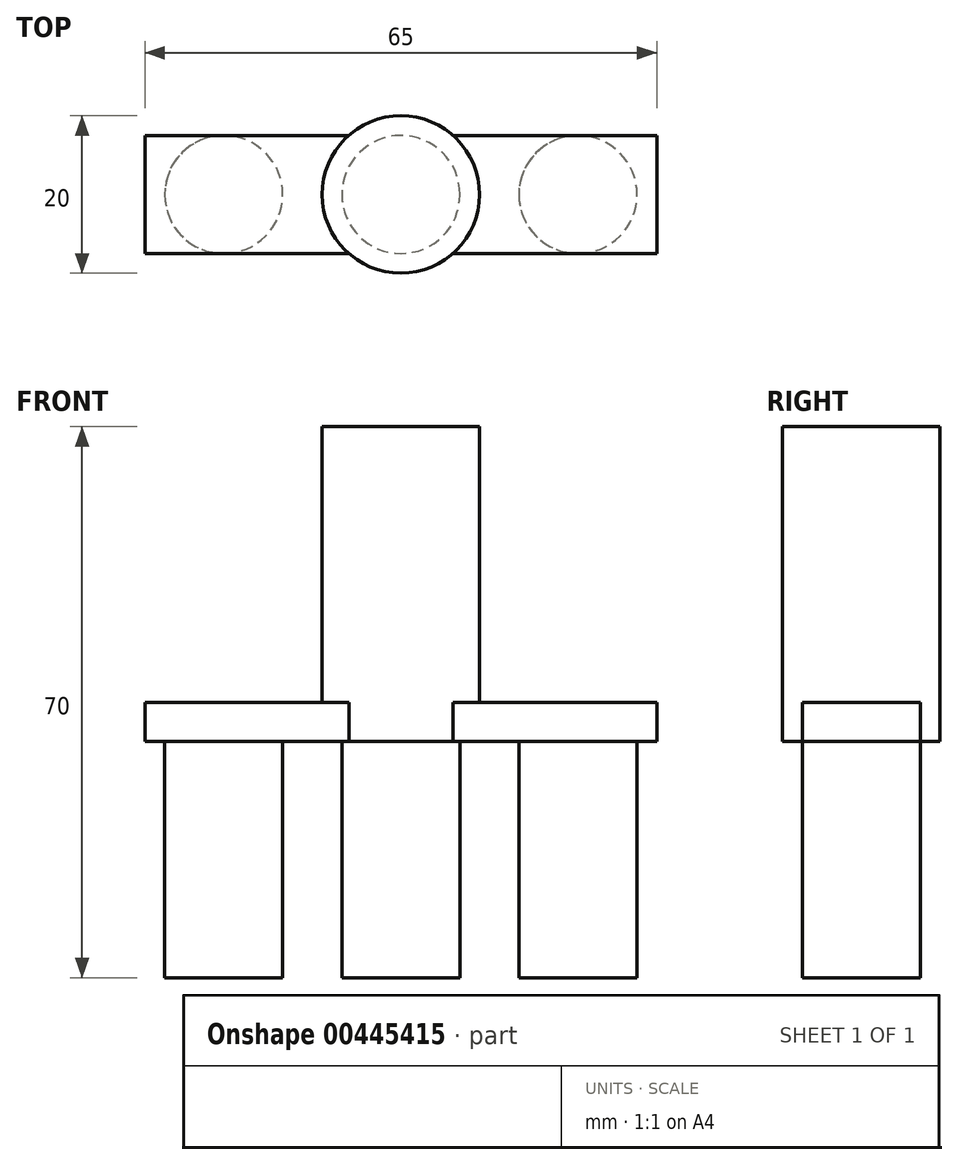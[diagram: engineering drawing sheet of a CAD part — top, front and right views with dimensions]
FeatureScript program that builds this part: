
annotation { "Feature Type Name" : "Feature", "Feature Type Description" : "" }
export const myFeature = defineFeature(function(context is Context, id is Id, definition is map)
    precondition{}
    {
        {
            var Q0;
            Q0=qCreatedBy(makeId("Top.planeOp"),FACE);
            var sketch = newSketch(context, id + "F0", { "sketchPlane" : qUnion([Q0])});
            skLineSegment(sketch, "E0.bottom", {"start": v(32.5, 7.5) * mm, "end": v(-32.5, 7.5) * mm});
            skLineSegment(sketch, "E0.top", {"start": v(32.5, -7.5) * mm, "end": v(-32.5, -7.5) * mm});
            skLineSegment(sketch, "E0.left", {"start": v(32.5, 7.5) * mm, "end": v(32.5, -7.5) * mm});
            skLineSegment(sketch, "E0.right", {"start": v(-32.5, 7.5) * mm, "end": v(-32.5, -7.5) * mm});
            skPoint(sketch, "E0.middle", {"position": v(0, 0) * mm});
            skSolve(sketch);
        }
        {
            var Q0;
            {var subQ5=sQuery(id+"F0.wireOp",EDGE,"E0.right");Q0=makeQuery(id+"F0.imprint","IMPRINT",FACE,{"disambiguationData":[TD([[makeQuery(id+"F0.imprint","IMPRINT",EDGE,{"derivedFrom":subQ5}),1.0]])]});}
            var Q1;
            {var subQ5=sQuery(id+"F0.wireOp",EDGE,"E0.left");Q1=makeQuery(id+"F0.imprint","IMPRINT",FACE,{"disambiguationData":[TD([[makeQuery(id+"F0.imprint","IMPRINT",EDGE,{"derivedFrom":subQ5}),-1.0]])]});}
            extrude(context, id + "F1", {"entities" : qUnion([Q0, Q1]), "oppositeDirection" : true, "depth" : 5 * mm});
        }
        {
            var Q0;
            Q0=makeQuery(id+"F1.opExtrude","CAP_FACE",FACE,{"disambiguationData":[OSD([sQuery(id+"F0.wireOp",EDGE,"E0.bottom"),sQuery(id+"F0.wireOp",EDGE,"E0.top"),sQuery(id+"F0.wireOp",EDGE,"E0.left"),sQuery(id+"F0.wireOp",EDGE,"E0.right")])],"isStart":false});
            var sketch = newSketch(context, id + "F2", { "sketchPlane" : qUnion([Q0])});
            skCircle(sketch, "E1", {"center": v(0, 0) * mm, "radius": 10 * mm});
            skSolve(sketch);
        }
        {
            var Q0;
            Q0 = qSketchRegion(id + "F2", true);
            extrude(context, id + "F3", {"entities" : qUnion([Q0]), "operationType" : NewBodyOperationType.ADD, "oppositeDirection" : true, "depth" : 40 * mm});
        }
        {
            var Q0;
            Q0=makeQuery(id+"F3.boolean.opBoolean","MERGE",FACE,{"derivedFrom":[makeQuery(id+"F1.opExtrude","CAP_FACE",FACE,{"disambiguationData":[OSD([sQuery(id+"F0.wireOp",EDGE,"E0.bottom"),sQuery(id+"F0.wireOp",EDGE,"E0.top"),sQuery(id+"F0.wireOp",EDGE,"E0.left"),sQuery(id+"F0.wireOp",EDGE,"E0.right")])],"isStart":false}),makeQuery(id+"F3.opExtrude","CAP_FACE",FACE,{"disambiguationData":[OSD([sQuery(id+"F2.wireOp",EDGE,"E1")])],"isStart":true})]});
            var sketch = newSketch(context, id + "F4", { "sketchPlane" : qUnion([Q0])});
            skCircle(sketch, "E2", {"center": v(0, 0) * mm, "radius": 7.5 * mm});
            skLineSegment(sketch, "E3", {"start": v(-7.5, 0) * mm, "end": v(-22.5, 0) * mm});
            skLineSegment(sketch, "E4", {"start": v(7.5, 0) * mm, "end": v(22.5, 0) * mm});
            skCircle(sketch, "E5", {"center": v(-22.5, 0) * mm, "radius": 7.5 * mm});
            skCircle(sketch, "E6", {"center": v(22.5, 0) * mm, "radius": 7.5 * mm});
            skSolve(sketch);
        }
        {
            var Q0;
            Q0 = qSketchRegion(id + "F4", true);
            extrude(context, id + "F5", {"entities" : qUnion([Q0]), "operationType" : NewBodyOperationType.ADD, "depth" : 30 * mm});
        }
    });
